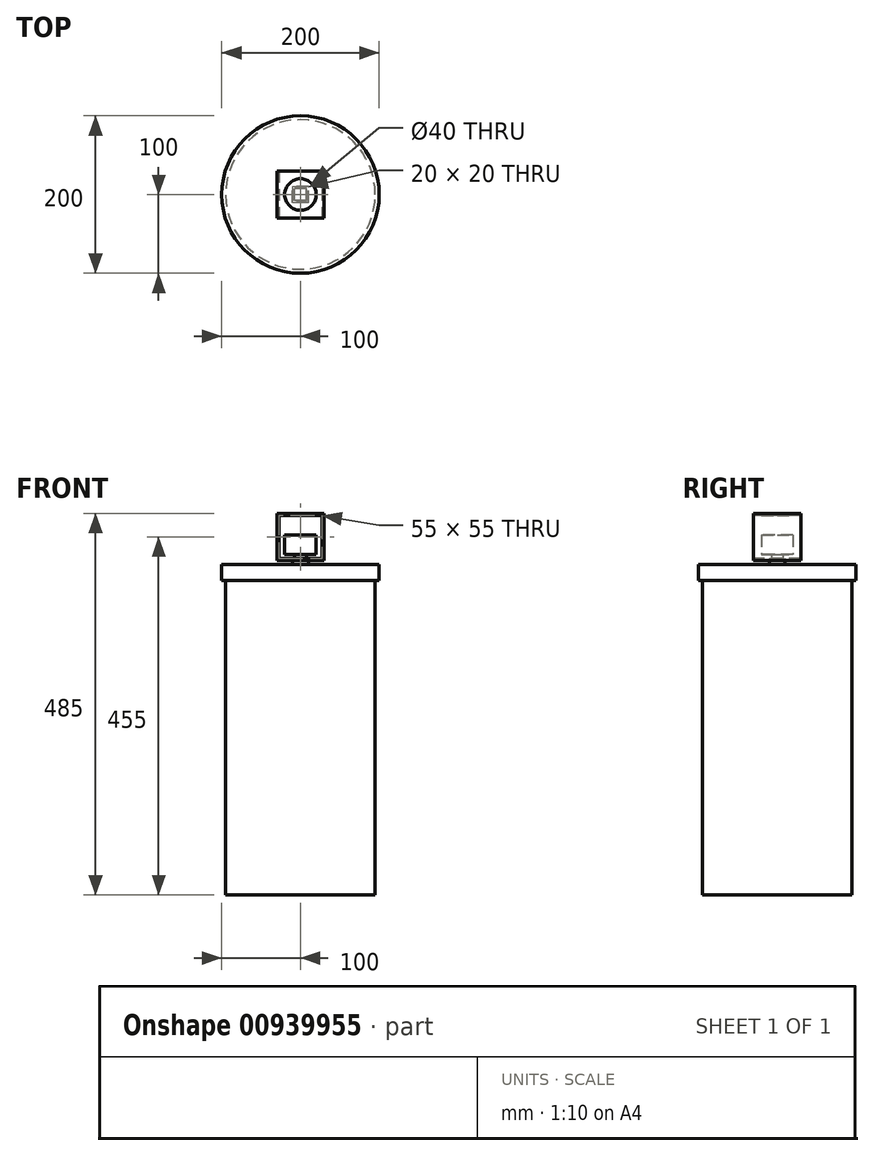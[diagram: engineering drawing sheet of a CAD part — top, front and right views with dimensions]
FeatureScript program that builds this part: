
annotation { "Feature Type Name" : "Feature", "Feature Type Description" : "" }
export const myFeature = defineFeature(function(context is Context, id is Id, definition is map)
    precondition{}
    {
        {
            var Q0;
            Q0=qCreatedBy(makeId("Top.planeOp"),FACE);
            var sketch = newSketch(context, id + "F0", { "sketchPlane" : qUnion([Q0])});
            skCircle(sketch, "E0", {"center": v(0, 0) * mm, "radius": 95 * mm});
            skSolve(sketch);
        }
        {
            var Q0;
            Q0=makeQuery(id+"F0.imprint","IMPRINT",FACE,{"disambiguationData":[TD([[makeQuery(id+"F0.imprint","IMPRINT",EDGE,{"derivedFrom":sQuery(id+"F0.wireOp",EDGE,"E0")}),1.0]])]});
            extrude(context, id + "F1", {"entities" : qUnion([Q0]), "depth" : 400 * mm, "offsetDistance" : 25 * mm});
        }
        {
            var Q0;
            Q0=makeQuery(id+"F1.opExtrude","CAP_FACE",FACE,{"disambiguationData":[OSD([sQuery(id+"F0.wireOp",EDGE,"E0")])],"isStart":false});
            var sketch = newSketch(context, id + "F2", { "sketchPlane" : qUnion([Q0])});
            skCircle(sketch, "E1", {"center": v(0, 0) * mm, "radius": 100 * mm});
            skSolve(sketch);
        }
        {
            var Q0;
            Q0=makeQuery(id+"F2.imprint","IMPRINT",FACE,{"disambiguationData":[TD([[makeQuery(id+"F2.imprint","IMPRINT",EDGE,{"derivedFrom":sQuery(id+"F2.wireOp",EDGE,"E1")}),1.0]])]});
            var Q1;
            Q1=makeQuery(id+"F2.imprint","IMPRINT",FACE,{"disambiguationData":[TD([[makeQuery(id+"F2.imprint","IMPRINT",EDGE,{"derivedFrom":makeQuery(id+"F1.opExtrude","CAP_EDGE",EDGE,{"disambiguationData":[OSD([sQuery(id+"F0.wireOp",EDGE,"E0")])],"isStart":false})}),1.0]])]});
            extrude(context, id + "F3", {"entities" : qUnion([Q0, Q1]), "operationType" : NewBodyOperationType.ADD, "depth" : 20 * mm, "offsetDistance" : 25 * mm});
        }
        {
            var Q0;
            Q0=makeQuery(id+"F3.opExtrude","CAP_FACE",FACE,{"disambiguationData":[OSD([sQuery(id+"F2.wireOp",EDGE,"E1")])],"isStart":false});
            var sketch = newSketch(context, id + "F4", { "sketchPlane" : qUnion([Q0])});
            skLineSegment(sketch, "E2.bottom", {"start": v(10, -10) * mm, "end": v(-10, -10) * mm});
            skLineSegment(sketch, "E2.top", {"start": v(10, 10) * mm, "end": v(-10, 10) * mm});
            skLineSegment(sketch, "E2.left", {"start": v(10, -10) * mm, "end": v(10, 10) * mm});
            skLineSegment(sketch, "E2.right", {"start": v(-10, -10) * mm, "end": v(-10, 10) * mm});
            skPoint(sketch, "E2.middle", {"position": v(0, 0) * mm});
            skSolve(sketch);
        }
        {
            var Q0;
            Q0=makeQuery(id+"F4.imprint","IMPRINT",FACE,{"disambiguationData":[TD([[makeQuery(id+"F4.imprint","IMPRINT",EDGE,{"derivedFrom":sQuery(id+"F4.wireOp",EDGE,"E2.bottom")}),-1.0]])]});
            extrude(context, id + "F5", {"entities" : qUnion([Q0]), "operationType" : NewBodyOperationType.ADD, "depth" : 5 * mm, "offsetDistance" : 25 * mm});
        }
        {
            var Q0;
            Q0=makeQuery(id+"F5.opExtrude","CAP_FACE",FACE,{"disambiguationData":[OSD([sQuery(id+"F4.wireOp",EDGE,"E2.bottom"),sQuery(id+"F4.wireOp",EDGE,"E2.top"),sQuery(id+"F4.wireOp",EDGE,"E2.left"),sQuery(id+"F4.wireOp",EDGE,"E2.right")])],"isStart":false});
            var sketch = newSketch(context, id + "F6", { "sketchPlane" : qUnion([Q0])});
            skLineSegment(sketch, "E3.bottom", {"start": v(30, -30) * mm, "end": v(-30, -30) * mm});
            skLineSegment(sketch, "E3.top", {"start": v(30, 30) * mm, "end": v(-30, 30) * mm});
            skLineSegment(sketch, "E3.left", {"start": v(30, -30) * mm, "end": v(30, 30) * mm});
            skLineSegment(sketch, "E3.right", {"start": v(-30, -30) * mm, "end": v(-30, 30) * mm});
            skPoint(sketch, "E3.middle", {"position": v(0, 0) * mm});
            skSolve(sketch);
        }
        {
            var Q0;
            Q0=makeQuery(id+"F6.imprint","IMPRINT",FACE,{"disambiguationData":[TD([[makeQuery(id+"F6.imprint","IMPRINT",EDGE,{"derivedFrom":sQuery(id+"F6.wireOp",EDGE,"E3.bottom")}),-1.0]])]});
            var sketch = newSketch(context, id + "F7", { "sketchPlane" : qUnion([Q0])});
            skSolve(sketch);
        }
        {
            var Q0;
            Q0=makeQuery(id+"F6.imprint","IMPRINT",FACE,{"disambiguationData":[TD([[makeQuery(id+"F6.imprint","IMPRINT",EDGE,{"derivedFrom":sQuery(id+"F6.wireOp",EDGE,"E3.bottom")}),-1.0]])]});
            var Q1;
            Q1=makeQuery(id+"F7.imprint","IMPRINT",FACE,{"disambiguationData":[TD([[makeQuery(id+"F7.imprint","IMPRINT",EDGE,{"derivedFrom":makeQuery(id+"F6.imprint","IMPRINT",EDGE,{"derivedFrom":makeQuery(id+"F5.opExtrude","CAP_EDGE",EDGE,{"disambiguationData":[OSD([sQuery(id+"F4.wireOp",EDGE,"E2.bottom")])],"isStart":false})})}),-1.0]])]});
            extrude(context, id + "F8", {"entities" : qUnion([Q0, Q1]), "operationType" : NewBodyOperationType.ADD, "depth" : 60 * mm, "offsetDistance" : 25 * mm});
        }
        {
            var Q0;
            Q0=makeQuery(id+"F8.opExtrude","SWEPT_FACE",FACE,{"disambiguationData":[OSD([sQuery(id+"F6.wireOp",EDGE,"E3.bottom")])]});
            var sketch = newSketch(context, id + "F9", { "sketchPlane" : qUnion([Q0])});
            skLineSegment(sketch, "E4", {"start": v(0, 425) * mm, "end": v(0, 427.5) * mm});
            skLineSegment(sketch, "E5.bottom", {"start": v(27.5, 427.5) * mm, "end": v(-27.5, 427.5) * mm});
            skLineSegment(sketch, "E5.top", {"start": v(27.5, 482.5) * mm, "end": v(-27.5, 482.5) * mm});
            skLineSegment(sketch, "E5.left", {"start": v(27.5, 427.5) * mm, "end": v(27.5, 482.5) * mm});
            skLineSegment(sketch, "E5.right", {"start": v(-27.5, 427.5) * mm, "end": v(-27.5, 482.5) * mm});
            skPoint(sketch, "E5.middle", {"position": v(0, 455) * mm});
            skLineSegment(sketch, "E6.trimOffspring", {"start": v(0, 482.5) * mm, "end": v(0, 485) * mm});
            skSolve(sketch);
        }
        {
            var Q0;
            {var subQ3=sQuery(id+"F9.wireOp",EDGE,"E5.left");Q0=makeQuery(id+"F9.imprint","IMPRINT",FACE,{"disambiguationData":[TD([[makeQuery(id+"F9.imprint","IMPRINT",EDGE,{"derivedFrom":subQ3}),1.0]])]});}
            extrude(context, id + "F10", {"entities" : qUnion([Q0]), "operationType" : NewBodyOperationType.REMOVE, "endBound" : BoundingType.THROUGH_ALL, "oppositeDirection" : true, "depth" : 25 * mm, "offsetDistance" : 25 * mm});
        }
        {
            var Q0;
            {var subQ0=sQuery(id+"F4.wireOp",EDGE,"E2.right");var subQ1=sQuery(id+"F4.wireOp",EDGE,"E2.left");var subQ2=sQuery(id+"F4.wireOp",EDGE,"E2.top");var subQ3=sQuery(id+"F4.wireOp",EDGE,"E2.bottom");Q0=makeQuery(id+"F8.boolean.opBoolean","MERGE",FACE,{"derivedFrom":[makeQuery(id+"F8.opExtrude","CAP_FACE",FACE,{"disambiguationData":[OSD([subQ3,subQ2,subQ1,subQ0,sQuery(id+"F6.wireOp",EDGE,"E3.bottom"),sQuery(id+"F6.wireOp",EDGE,"E3.top"),sQuery(id+"F6.wireOp",EDGE,"E3.left"),sQuery(id+"F6.wireOp",EDGE,"E3.right")])],"isStart":false}),makeQuery(id+"F8.opExtrude","CAP_FACE",FACE,{"disambiguationData":[OSD([subQ3,subQ2,subQ1,subQ0])],"isStart":false})]});}
            var sketch = newSketch(context, id + "F11", { "sketchPlane" : qUnion([Q0])});
            skCircle(sketch, "E7", {"center": v(0, 0) * mm, "radius": 20 * mm});
            skSolve(sketch);
        }
        {
            var Q0;
            Q0=makeQuery(id+"F11.imprint","IMPRINT",FACE,{"disambiguationData":[TD([[makeQuery(id+"F11.imprint","IMPRINT",EDGE,{"derivedFrom":sQuery(id+"F11.wireOp",EDGE,"E7")}),1.0]])]});
            extrude(context, id + "F12", {"entities" : qUnion([Q0]), "operationType" : NewBodyOperationType.REMOVE, "oppositeDirection" : true, "depth" : 25 * mm, "offsetDistance" : 25 * mm});
        }
        {
            var Q0;
            Q0=makeQuery(id+"F10.boolean.opBoolean","COPY",FACE,{"derivedFrom":makeQuery(id+"F10.opExtrude","SWEPT_FACE",FACE,{"disambiguationData":[OSD([sQuery(id+"F9.wireOp",EDGE,"E5.bottom")])]})});
            var sketch = newSketch(context, id + "F13", { "sketchPlane" : qUnion([Q0])});
            skLineSegment(sketch, "E8.bottom", {"start": v(7.5, -7.5) * mm, "end": v(-7.5, -7.5) * mm});
            skLineSegment(sketch, "E8.top", {"start": v(7.5, 7.5) * mm, "end": v(-7.5, 7.5) * mm});
            skLineSegment(sketch, "E8.left", {"start": v(7.5, -7.5) * mm, "end": v(7.5, 7.5) * mm});
            skLineSegment(sketch, "E8.right", {"start": v(-7.5, -7.5) * mm, "end": v(-7.5, 7.5) * mm});
            skPoint(sketch, "E8.middle", {"position": v(0, 0) * mm});
            skSolve(sketch);
        }
        {
            var Q0;
            Q0=makeQuery(id+"F13.imprint","IMPRINT",FACE,{"disambiguationData":[TD([[makeQuery(id+"F13.imprint","IMPRINT",EDGE,{"derivedFrom":sQuery(id+"F13.wireOp",EDGE,"E8.bottom")}),-1.0]])]});
            extrude(context, id + "F14", {"entities" : qUnion([Q0]), "operationType" : NewBodyOperationType.ADD, "depth" : 5 * mm, "offsetDistance" : 25 * mm});
        }
        {
            var Q0;
            Q0=makeQuery(id+"F14.opExtrude","CAP_FACE",FACE,{"disambiguationData":[OSD([sQuery(id+"F13.wireOp",EDGE,"E8.bottom"),sQuery(id+"F13.wireOp",EDGE,"E8.top"),sQuery(id+"F13.wireOp",EDGE,"E8.left"),sQuery(id+"F13.wireOp",EDGE,"E8.right")])],"isStart":false});
            var sketch = newSketch(context, id + "F15", { "sketchPlane" : qUnion([Q0])});
            skCircle(sketch, "E9", {"center": v(0, 0) * mm, "radius": 20 * mm});
            skSolve(sketch);
        }
        {
            var Q0;
            Q0=makeQuery(id+"F15.imprint","IMPRINT",FACE,{"disambiguationData":[TD([[makeQuery(id+"F15.imprint","IMPRINT",EDGE,{"derivedFrom":makeQuery(id+"F14.opExtrude","CAP_EDGE",EDGE,{"disambiguationData":[OSD([sQuery(id+"F13.wireOp",EDGE,"E8.bottom")])],"isStart":false})}),-1.0]])]});
            var Q1;
            Q1=makeQuery(id+"F15.imprint","IMPRINT",FACE,{"disambiguationData":[TD([[makeQuery(id+"F15.imprint","IMPRINT",EDGE,{"derivedFrom":sQuery(id+"F15.wireOp",EDGE,"E9")}),1.0]])]});
            extrude(context, id + "F16", {"entities" : qUnion([Q0, Q1]), "operationType" : NewBodyOperationType.ADD, "depth" : 25 * mm, "offsetDistance" : 25 * mm});
        }
    });
